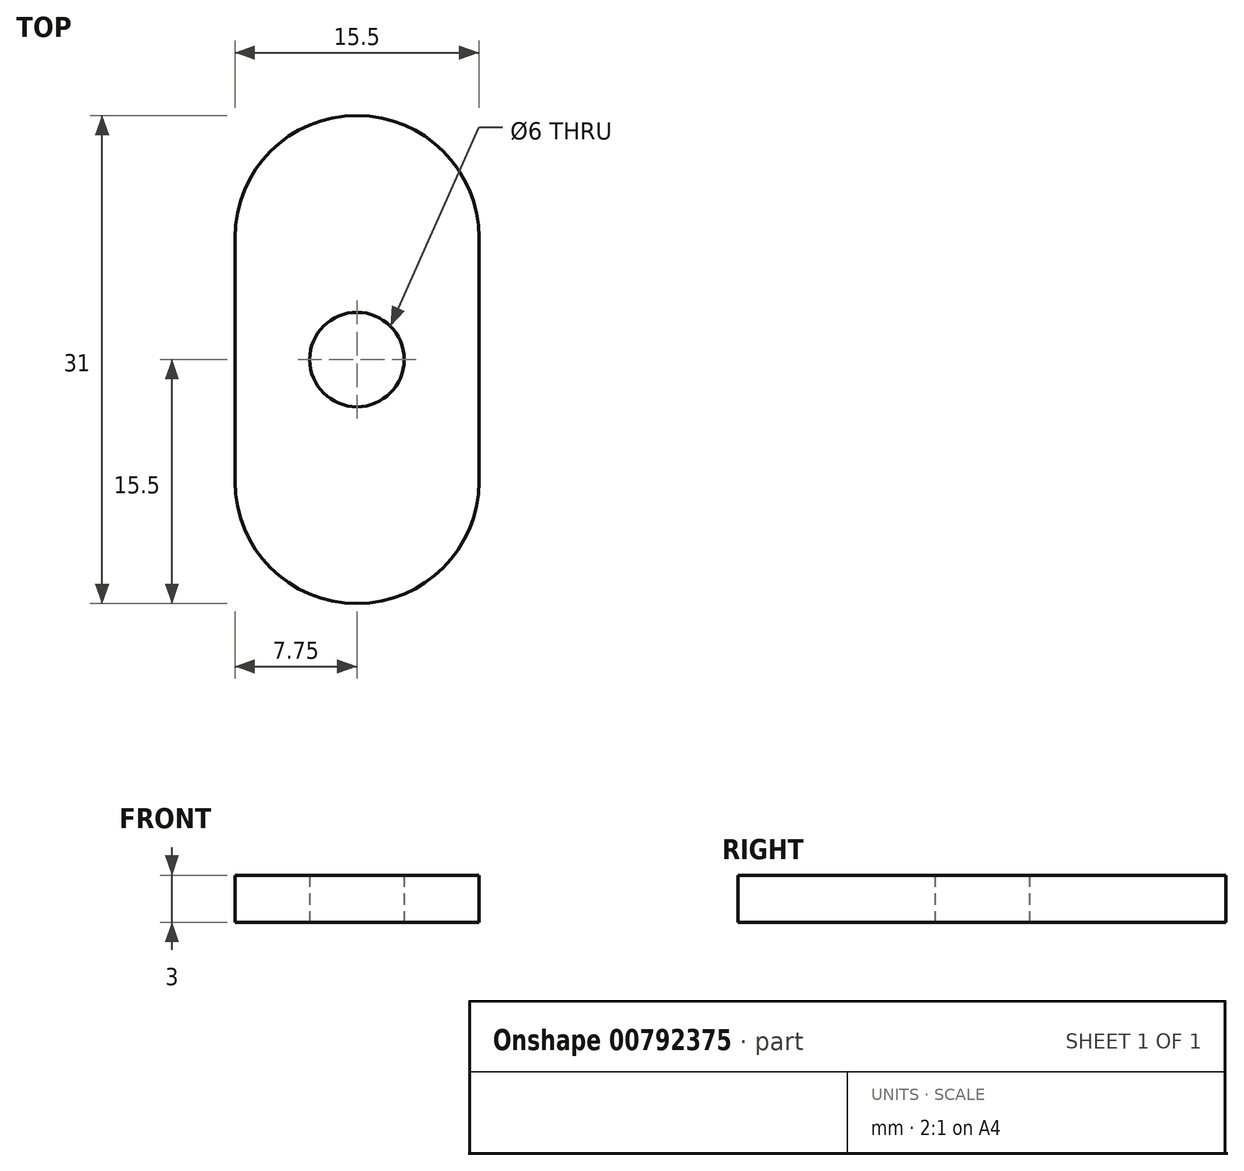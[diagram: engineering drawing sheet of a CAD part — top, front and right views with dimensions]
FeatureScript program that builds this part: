
annotation { "Feature Type Name" : "Feature", "Feature Type Description" : "" }
export const myFeature = defineFeature(function(context is Context, id is Id, definition is map)
    precondition{}
    {
        {
            var Q0;
            Q0=qCreatedBy(makeId("Top.planeOp"),FACE);
            var sketch = newSketch(context, id + "F0", { "sketchPlane" : qUnion([Q0])});
            skLineSegment(sketch, "E0.left", {"start": v(7.75, 7.75) * mm, "end": v(7.75, -7.75) * mm});
            skLineSegment(sketch, "E0.right", {"start": v(-7.75, 7.75) * mm, "end": v(-7.75, -7.75) * mm});
            skPoint(sketch, "E0.middle", {"position": v(0, 0) * mm});
            skArc(sketch, "E1", {"start": v(-7.75, 7.75) * mm, "mid": v(0, 15.5) * mm, "end": v(7.75, 7.75) * mm});
            skArc(sketch, "E2", {"start": v(7.75, -7.75) * mm, "mid": v(0, -15.5) * mm, "end": v(-7.75, -7.75) * mm});
            skCircle(sketch, "E3", {"center": v(0, 0) * mm, "radius": 3 * mm});
            skSolve(sketch);
        }
        {
            var Q0;
            Q0 = qSketchRegion(id + "F0", true);
            extrude(context, id + "F1", {"entities" : qUnion([Q0]), "depth" : 3 * mm, "offsetDistance" : 25 * mm});
        }
    });
